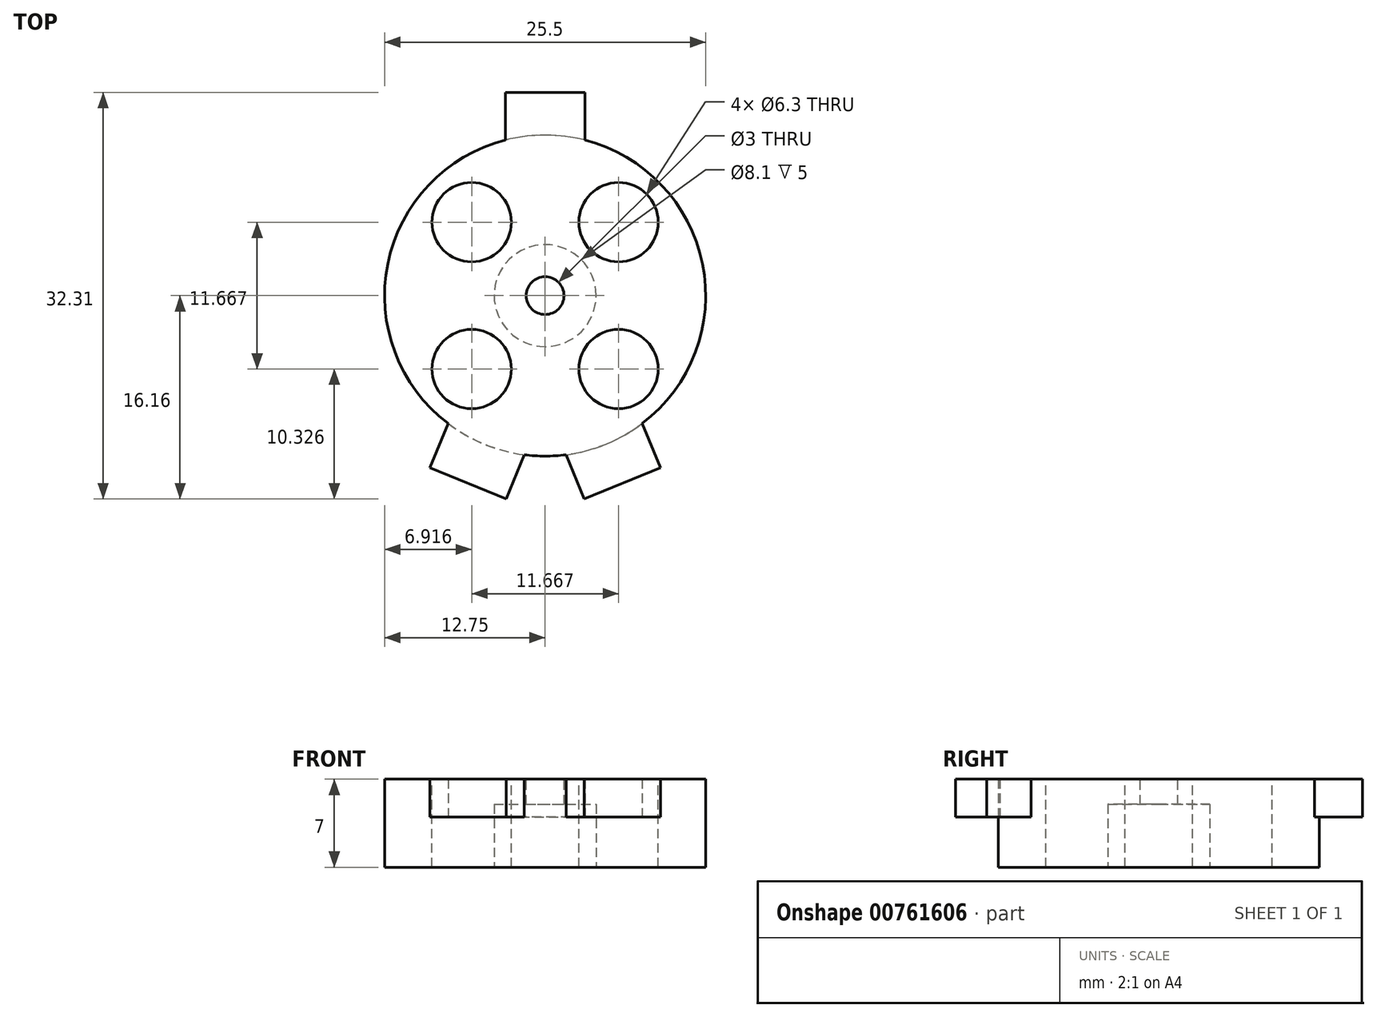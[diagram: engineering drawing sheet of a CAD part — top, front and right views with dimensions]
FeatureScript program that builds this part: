
annotation { "Feature Type Name" : "Feature", "Feature Type Description" : "" }
export const myFeature = defineFeature(function(context is Context, id is Id, definition is map)
    precondition{}
    {
        {
            var Q0;
            Q0=qCreatedBy(makeId("Top.planeOp"),FACE);
            var sketch = newSketch(context, id + "F0", { "sketchPlane" : qUnion([Q0])});
            skArc(sketch, "E0", {"start": v(7.7, -10.16) * mm, "mid": v(12.5, 2.53) * mm, "end": v(3.15, 12.35) * mm});
            skLineSegment(sketch, "E1", {"start": v(0, 12.75) * mm, "end": v(0, -12.75) * mm, "construction": true});
            skLineSegment(sketch, "E2", {"start": v(-3.15, 16.15) * mm, "end": v(0, 16.15) * mm});
            skLineSegment(sketch, "E3", {"start": v(0, 16.15) * mm, "end": v(3.15, 16.15) * mm});
            skLineSegment(sketch, "E4", {"start": v(-3.15, 16.15) * mm, "end": v(-3.15, 12.35) * mm});
            skLineSegment(sketch, "E5", {"start": v(3.15, 16.15) * mm, "end": v(3.15, 12.35) * mm});
            skLineSegment(sketch, "E6", {"start": v(1.66, -12.64) * mm, "end": v(7.7, -10.16) * mm, "construction": true});
            skLineSegment(sketch, "E7", {"start": v(1.66, -12.64) * mm, "end": v(3.1, -16.16) * mm});
            skLineSegment(sketch, "E8", {"start": v(7.7, -10.16) * mm, "end": v(9.15, -13.67) * mm});
            skLineSegment(sketch, "E9", {"start": v(3.1, -16.16) * mm, "end": v(9.15, -13.67) * mm});
            skLineSegment(sketch, "E10.MirrorCS", {"start": v(-1.66, -12.64) * mm, "end": v(-3.1, -16.16) * mm});
            skLineSegment(sketch, "E11.MirrorCS", {"start": v(-3.1, -16.16) * mm, "end": v(-9.15, -13.67) * mm});
            skLineSegment(sketch, "E12.MirrorCS", {"start": v(-7.7, -10.16) * mm, "end": v(-9.15, -13.67) * mm});
            skArc(sketch, "E13.trimOffspring", {"start": v(-1.66, -12.64) * mm, "mid": v(0, -12.75) * mm, "end": v(1.66, -12.64) * mm});
            skArc(sketch, "E14.trimOffspring", {"start": v(-3.15, 12.35) * mm, "mid": v(-12.5, 2.53) * mm, "end": v(-7.7, -10.16) * mm});
            skLineSegment(sketch, "E15", {"start": v(-1.66, -12.64) * mm, "end": v(1.66, -12.64) * mm, "construction": true});
            skLineSegment(sketch, "E16", {"start": v(-3.1, -16.16) * mm, "end": v(3.1, -16.16) * mm, "construction": true});
            skLineSegment(sketch, "E17", {"start": v(-9.15, -13.67) * mm, "end": v(9.15, -13.67) * mm, "construction": true});
            skLineSegment(sketch, "E18", {"start": v(-7.7, -10.16) * mm, "end": v(7.7, -10.16) * mm, "construction": true});
            skSolve(sketch);
        }
        {
            var Q0;
            Q0=qSketchRegion(id+"F0",true);
            extrude(context, id + "F1", {"entities" : qUnion([Q0]), "depth" : 3 * mm, "offsetDistance" : 25 * mm});
        }
        {
            var Q0;
            Q0=makeQuery(id+"F1.opExtrude","CAP_FACE",FACE,{"disambiguationData":[OSD([sQuery(id+"F0.wireOp",EDGE,"E0"),sQuery(id+"F0.wireOp",EDGE,"E2"),sQuery(id+"F0.wireOp",EDGE,"E3"),sQuery(id+"F0.wireOp",EDGE,"E4"),sQuery(id+"F0.wireOp",EDGE,"E5"),sQuery(id+"F0.wireOp",EDGE,"E7"),sQuery(id+"F0.wireOp",EDGE,"E8"),sQuery(id+"F0.wireOp",EDGE,"E9"),sQuery(id+"F0.wireOp",EDGE,"E10.MirrorCS"),sQuery(id+"F0.wireOp",EDGE,"E11.MirrorCS"),sQuery(id+"F0.wireOp",EDGE,"E12.MirrorCS"),sQuery(id+"F0.wireOp",EDGE,"E13.trimOffspring"),sQuery(id+"F0.wireOp",EDGE,"E14.trimOffspring")])],"isStart":true});
            var sketch = newSketch(context, id + "F2", { "sketchPlane" : qUnion([Q0])});
            skCircle(sketch, "E19", {"center": v(0, 0) * mm, "radius": 12.75 * mm});
            skSolve(sketch);
        }
        {
            var Q0;
            Q0 = qSketchRegion(id + "F2", true);
            extrude(context, id + "F3", {"entities" : qUnion([Q0]), "operationType" : NewBodyOperationType.ADD, "depth" : 4 * mm, "offsetDistance" : 25 * mm});
        }
        {
            var Q0;
            Q0=makeQuery(id+"F1.opExtrude","CAP_FACE",FACE,{"disambiguationData":[OSD([sQuery(id+"F0.wireOp",EDGE,"E0"),sQuery(id+"F0.wireOp",EDGE,"E2"),sQuery(id+"F0.wireOp",EDGE,"E3"),sQuery(id+"F0.wireOp",EDGE,"E4"),sQuery(id+"F0.wireOp",EDGE,"E5"),sQuery(id+"F0.wireOp",EDGE,"E7"),sQuery(id+"F0.wireOp",EDGE,"E8"),sQuery(id+"F0.wireOp",EDGE,"E9"),sQuery(id+"F0.wireOp",EDGE,"E10.MirrorCS"),sQuery(id+"F0.wireOp",EDGE,"E11.MirrorCS"),sQuery(id+"F0.wireOp",EDGE,"E12.MirrorCS"),sQuery(id+"F0.wireOp",EDGE,"E13.trimOffspring"),sQuery(id+"F0.wireOp",EDGE,"E14.trimOffspring")])],"isStart":false});
            var sketch = newSketch(context, id + "F4", { "sketchPlane" : qUnion([Q0])});
            skLineSegment(sketch, "E20", {"start": v(-12.75, 0) * mm, "end": v(0, 0) * mm, "construction": true});
            skLineSegment(sketch, "E21", {"start": v(0, 0) * mm, "end": v(-2.65, 2.65) * mm, "construction": true});
            skLineSegment(sketch, "E22", {"start": v(0, 0) * mm, "end": v(9.02, -9.02) * mm, "construction": true});
            skLineSegment(sketch, "E23.MirrorCS", {"start": v(0, 0) * mm, "end": v(9.02, 9.02) * mm, "construction": true});
            skLineSegment(sketch, "E24.MirrorCS", {"start": v(0, 0) * mm, "end": v(-9.02, -9.02) * mm, "construction": true});
            skCircle(sketch, "E25", {"center": v(-5.83, 5.83) * mm, "radius": 3.15 * mm});
            skCircle(sketch, "E26.1.0", {"center": v(-5.83, -5.83) * mm, "radius": 3.15 * mm});
            skCircle(sketch, "E26.2.0", {"center": v(5.83, -5.83) * mm, "radius": 3.15 * mm});
            skCircle(sketch, "E26.3.0", {"center": v(5.83, 5.83) * mm, "radius": 3.15 * mm});
            skLineSegment(sketch, "E27", {"start": v(-2.65, 2.65) * mm, "end": v(-9.02, 9.02) * mm, "construction": true});
            skCircle(sketch, "E28", {"center": v(0, 0) * mm, "radius": 1.5 * mm});
            skSolve(sketch);
        }
        {
            var Q0;
            Q0=qSketchRegion(id+"F4",true);
            var Q1;
            Q1=makeQuery(id+"F1.opExtrude","CAP_FACE",FACE,{"disambiguationData":[OSD([sQuery(id+"F0.wireOp",EDGE,"E0"),sQuery(id+"F0.wireOp",EDGE,"E2"),sQuery(id+"F0.wireOp",EDGE,"E3"),sQuery(id+"F0.wireOp",EDGE,"E4"),sQuery(id+"F0.wireOp",EDGE,"E5"),sQuery(id+"F0.wireOp",EDGE,"E7"),sQuery(id+"F0.wireOp",EDGE,"E8"),sQuery(id+"F0.wireOp",EDGE,"E9"),sQuery(id+"F0.wireOp",EDGE,"E10.MirrorCS"),sQuery(id+"F0.wireOp",EDGE,"E11.MirrorCS"),sQuery(id+"F0.wireOp",EDGE,"E12.MirrorCS"),sQuery(id+"F0.wireOp",EDGE,"E13.trimOffspring"),sQuery(id+"F0.wireOp",EDGE,"E14.trimOffspring")])],"isStart":true});
            extrude(context, id + "F5", {"entities" : qUnion([Q0]), "operationType" : NewBodyOperationType.REMOVE, "oppositeDirection" : true, "depth" : 25 * mm, "endBoundEntityFace" : qUnion([Q1]), "offsetDistance" : 25 * mm});
        }
        {
            var Q0;
            Q0=makeQuery(id+"F3.opExtrude","CAP_FACE",FACE,{"disambiguationData":[OSD([sQuery(id+"F2.wireOp",EDGE,"E19")])],"isStart":false});
            var sketch = newSketch(context, id + "F6", { "sketchPlane" : qUnion([Q0])});
            skCircle(sketch, "E29", {"center": v(0, 0) * mm, "radius": 4.05 * mm});
            skSolve(sketch);
        }
        {
            var Q0;
            Q0 = qSketchRegion(id + "F6", true);
            extrude(context, id + "F7", {"entities" : qUnion([Q0]), "operationType" : NewBodyOperationType.REMOVE, "oppositeDirection" : true, "depth" : 5 * mm, "offsetDistance" : 25 * mm});
        }
    });
